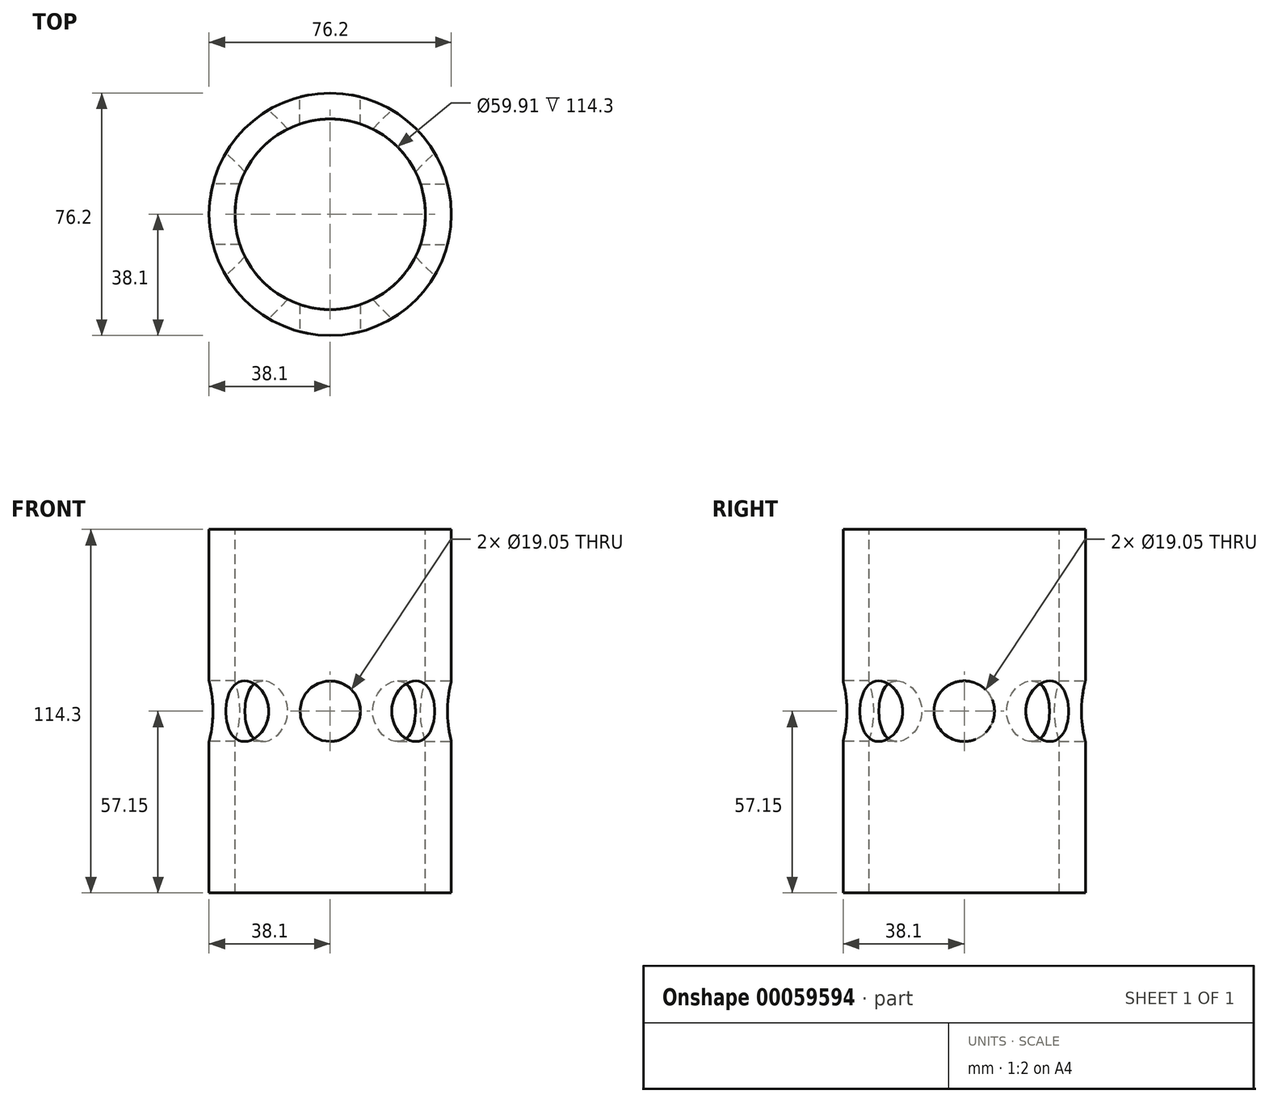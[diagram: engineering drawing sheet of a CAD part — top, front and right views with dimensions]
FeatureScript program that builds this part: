
annotation { "Feature Type Name" : "Feature", "Feature Type Description" : "" }
export const myFeature = defineFeature(function(context is Context, id is Id, definition is map)
    precondition{}
    {
        {
            var Q0;
            Q0=qCreatedBy(makeId("Front.planeOp"),FACE);
            var sketch = newSketch(context, id + "F0", { "sketchPlane" : qUnion([Q0])});
            skLineSegment(sketch, "E0.bottom", {"start": v(-38.1, 57.15) * mm, "end": v(0, 57.15) * mm});
            skLineSegment(sketch, "E0.top", {"start": v(-38.1, -57.15) * mm, "end": v(0, -57.15) * mm});
            skLineSegment(sketch, "E0.left", {"start": v(-38.1, 57.15) * mm, "end": v(-38.1, -57.15) * mm});
            skLineSegment(sketch, "E0.right", {"start": v(0, 57.15) * mm, "end": v(0, -57.15) * mm});
            skSolve(sketch);
        }
        {
            var Q0;
            Q0=makeQuery(id+"F0.imprint","IMPRINT",FACE,{"disambiguationData":[TD([[makeQuery(id+"F0.imprint","IMPRINT",EDGE,{"derivedFrom":sQuery(id+"F0.wireOp",EDGE,"E0.bottom")}),-1.0]])]});
            var Q1;
            Q1=sQuery(id+"F0.wireOp",EDGE,"E0.right");
            revolve(context, id + "F1", {"entities" : qUnion([Q0]), "axis" : qUnion([Q1]), "revolveType" : RevolveType.FULL});
        }
        {
            var Q0;
            Q0=qCreatedBy(makeId("Front.planeOp"),FACE);
            cPlane(context, id + "F2", {"entities" : qUnion([Q0]), "cplaneType" : CPlaneType.OFFSET, "offset" : 38.1 * mm, "width" : 152.4 * mm, "height" : 152.4 * mm});
        }
        {
            var Q0;
            Q0=qCreatedBy(id+"F2.planeOp",FACE);
            var sketch = newSketch(context, id + "F3", { "sketchPlane" : qUnion([Q0])});
            skCircle(sketch, "E1", {"center": v(0, 0) * mm, "radius": 9.53 * mm});
            skSolve(sketch);
        }
        {
            var Q0;
            Q0=makeQuery(id+"F3.imprint","IMPRINT",FACE,{"disambiguationData":[TD([[makeQuery(id+"F3.imprint","IMPRINT",EDGE,{"derivedFrom":sQuery(id+"F3.wireOp",EDGE,"E1")}),1.0]])]});
            var Q1;
            Q1=sQuery(id+"F3.wireOp",EDGE,"E1");
            extrude(context, id + "F4", {"entities" : qUnion([Q0]), "surfaceEntities" : qUnion([Q1]), "oppositeDirection" : true, "depth" : 10.16 * mm});
        }
        {
            var Q0;
            Q0=makeQuery(id+"F4.opExtrude","SWEPT_BODY",BODY,{"disambiguationData":[OSD([sQuery(id+"F3.wireOp",EDGE,"E1")])]});
            var Q1;
            Q1=makeQuery(id+"F1.opRevolve","SWEPT_EDGE",EDGE,{"disambiguationData":[OSD([sQuery(id+"F0.wireOp",EDGE,"E0.bottom"),sQuery(id+"F0.wireOp",EDGE,"E0.left")])]});
            circularPattern(context, id + "F5", {"entities" : qUnion([Q0]), "axis" : qUnion([Q1]), "angle" : 360 * degree, "instanceCount" : 8, "equalSpace" : true});
        }
        {
            var Q0;
            Q0=makeQuery(id+"F4.opExtrude","SWEPT_BODY",BODY,{"disambiguationData":[OSD([sQuery(id+"F3.wireOp",EDGE,"E1")])]});
            var Q1;
            Q1=makeQuery(id+"F5.opPattern","COPY",BODY,{"derivedFrom":makeQuery(id+"F4.opExtrude","SWEPT_BODY",BODY,{"disambiguationData":[OSD([sQuery(id+"F3.wireOp",EDGE,"E1")])]}),"instanceName":"1"});
            var Q2;
            Q2=makeQuery(id+"F5.opPattern","COPY",BODY,{"derivedFrom":makeQuery(id+"F4.opExtrude","SWEPT_BODY",BODY,{"disambiguationData":[OSD([sQuery(id+"F3.wireOp",EDGE,"E1")])]}),"instanceName":"2"});
            var Q3;
            Q3=makeQuery(id+"F5.opPattern","COPY",BODY,{"derivedFrom":makeQuery(id+"F4.opExtrude","SWEPT_BODY",BODY,{"disambiguationData":[OSD([sQuery(id+"F3.wireOp",EDGE,"E1")])]}),"instanceName":"3"});
            var Q4;
            Q4=makeQuery(id+"F5.opPattern","COPY",BODY,{"derivedFrom":makeQuery(id+"F4.opExtrude","SWEPT_BODY",BODY,{"disambiguationData":[OSD([sQuery(id+"F3.wireOp",EDGE,"E1")])]}),"instanceName":"4"});
            var Q5;
            Q5=makeQuery(id+"F5.opPattern","COPY",BODY,{"derivedFrom":makeQuery(id+"F4.opExtrude","SWEPT_BODY",BODY,{"disambiguationData":[OSD([sQuery(id+"F3.wireOp",EDGE,"E1")])]}),"instanceName":"5"});
            var Q6;
            Q6=makeQuery(id+"F5.opPattern","COPY",BODY,{"derivedFrom":makeQuery(id+"F4.opExtrude","SWEPT_BODY",BODY,{"disambiguationData":[OSD([sQuery(id+"F3.wireOp",EDGE,"E1")])]}),"instanceName":"6"});
            var Q7;
            Q7=makeQuery(id+"F5.opPattern","COPY",BODY,{"derivedFrom":makeQuery(id+"F4.opExtrude","SWEPT_BODY",BODY,{"disambiguationData":[OSD([sQuery(id+"F3.wireOp",EDGE,"E1")])]}),"instanceName":"7"});
            var Q8;
            Q8=makeQuery(id+"F5.opPattern","COPY",BODY,{"derivedFrom":makeQuery(id+"F4.opExtrude","SWEPT_BODY",BODY,{"disambiguationData":[OSD([sQuery(id+"F3.wireOp",EDGE,"E1")])]}),"instanceName":"8"});
            var Q9;
            Q9=makeQuery(id+"F5.opPattern","COPY",BODY,{"derivedFrom":makeQuery(id+"F4.opExtrude","SWEPT_BODY",BODY,{"disambiguationData":[OSD([sQuery(id+"F3.wireOp",EDGE,"E1")])]}),"instanceName":"9"});
            var Q10;
            Q10=makeQuery(id+"F1.opRevolve","SWEPT_BODY",BODY,{"disambiguationData":[OSD([sQuery(id+"F0.wireOp",EDGE,"E0.bottom"),sQuery(id+"F0.wireOp",EDGE,"E0.top"),sQuery(id+"F0.wireOp",EDGE,"E0.left"),sQuery(id+"F0.wireOp",EDGE,"E0.right")])]});
            booleanBodies(context, id + "F6", {"operationType" : BooleanOperationType.SUBTRACTION, "tools" : qUnion([Q0, Q1, Q2, Q3, Q4, Q5, Q6, Q7, Q8, Q9]), "targets" : qUnion([Q10])});
        }
        {
            var Q0;
            Q0=makeQuery(id+"F1.opRevolve","SWEPT_FACE",FACE,{"disambiguationData":[OSD([sQuery(id+"F0.wireOp",EDGE,"E0.bottom")])]});
            cPlane(context, id + "F7", {"entities" : qUnion([Q0]), "cplaneType" : CPlaneType.OFFSET, "offset" : 0 * mm, "width" : 152.4 * mm, "height" : 152.4 * mm});
        }
        {
            var Q0;
            Q0=qCreatedBy(id+"F7.planeOp",FACE);
            var sketch = newSketch(context, id + "F8", { "sketchPlane" : qUnion([Q0])});
            skCircle(sketch, "E2", {"center": v(0, 0) * mm, "radius": 29.96 * mm});
            skSolve(sketch);
        }
        {
            var Q0;
            Q0=makeQuery(id+"F8.imprint","IMPRINT",FACE,{"disambiguationData":[TD([[makeQuery(id+"F8.imprint","IMPRINT",EDGE,{"derivedFrom":sQuery(id+"F8.wireOp",EDGE,"E2")}),1.0]])]});
            var Q1;
            Q1=sQuery(id+"F8.wireOp",EDGE,"E2");
            extrude(context, id + "F9", {"entities" : qUnion([Q0]), "operationType" : NewBodyOperationType.REMOVE, "surfaceEntities" : qUnion([Q1]), "endBound" : BoundingType.THROUGH_ALL, "oppositeDirection" : true, "depth" : 25.4 * mm});
        }
    });
